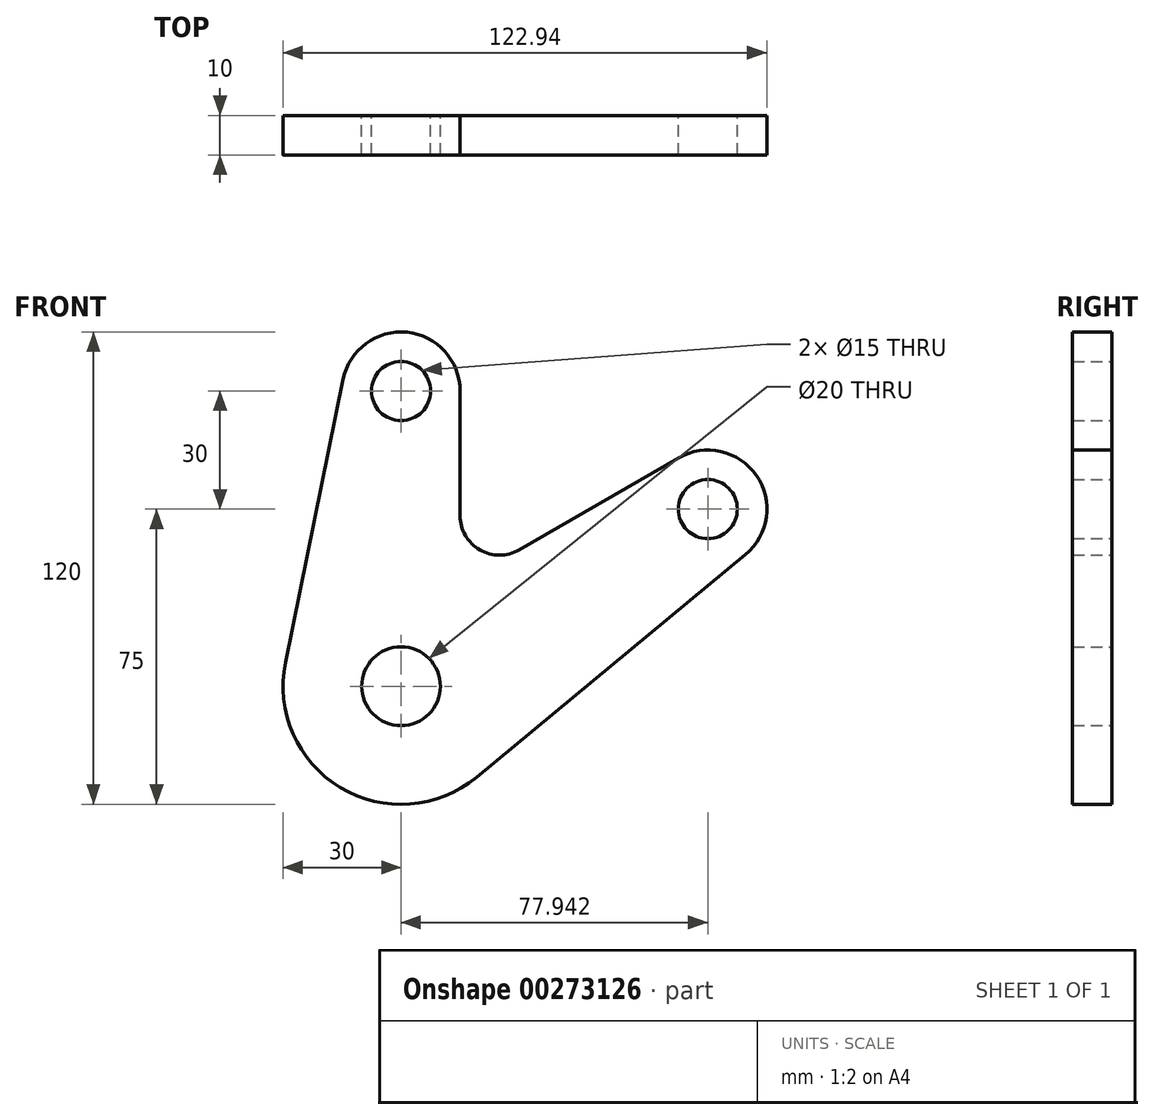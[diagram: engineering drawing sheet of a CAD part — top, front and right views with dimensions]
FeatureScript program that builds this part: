
annotation { "Feature Type Name" : "Feature", "Feature Type Description" : "" }
export const myFeature = defineFeature(function(context is Context, id is Id, definition is map)
    precondition{}
    {
        {
            var Q0;
            Q0=qCreatedBy(makeId("Front.planeOp"),FACE);
            var sketch = newSketch(context, id + "F0", { "sketchPlane" : qUnion([Q0])});
            skCircle(sketch, "E0", {"center": v(0, 75) * mm, "radius": 7.5 * mm});
            skCircle(sketch, "E1", {"center": v(77.94, 45) * mm, "radius": 7.5 * mm});
            skCircle(sketch, "E2", {"center": v(0, 0) * mm, "radius": 10 * mm});
            skArc(sketch, "E3", {"start": v(-29.4, 6) * mm, "mid": v(-15.44, -25.72) * mm, "end": v(19.12, -23.12) * mm});
            skArc(sketch, "E4", {"start": v(15, 75) * mm, "mid": v(1.5, 89.92) * mm, "end": v(-14.7, 78) * mm});
            skArc(sketch, "E5", {"start": v(87.5, 33.44) * mm, "mid": v(90.26, 53.56) * mm, "end": v(70.44, 58) * mm});
            skLineSegment(sketch, "E6", {"start": v(-14.7, 78) * mm, "end": v(-29.4, 6) * mm});
            skLineSegment(sketch, "E7", {"start": v(87.5, 33.44) * mm, "end": v(19.12, -23.12) * mm});
            skArc(sketch, "E8", {"start": v(15, 43.3) * mm, "mid": v(20, 34.64) * mm, "end": v(30, 34.64) * mm});
            skLineSegment(sketch, "E9", {"start": v(70.44, 58) * mm, "end": v(30, 34.64) * mm});
            skLineSegment(sketch, "E10", {"start": v(15, 75) * mm, "end": v(15, 43.3) * mm});
            skLineSegment(sketch, "E11", {"start": v(77.94, 45) * mm, "end": v(0, 0) * mm, "construction": true});
            skLineSegment(sketch, "E12", {"start": v(0, 75) * mm, "end": v(0, 0) * mm, "construction": true});
            skSolve(sketch);
        }
        {
            var Q0;
            Q0=makeQuery(id+"F0.imprint","IMPRINT",FACE,{"disambiguationData":[TD([[makeQuery(id+"F0.imprint","IMPRINT",EDGE,{"derivedFrom":sQuery(id+"F0.wireOp",EDGE,"E0")}),-1.0]])]});
            extrude(context, id + "F1", {"entities" : qUnion([Q0]), "depth" : 10 * mm});
        }
    });
